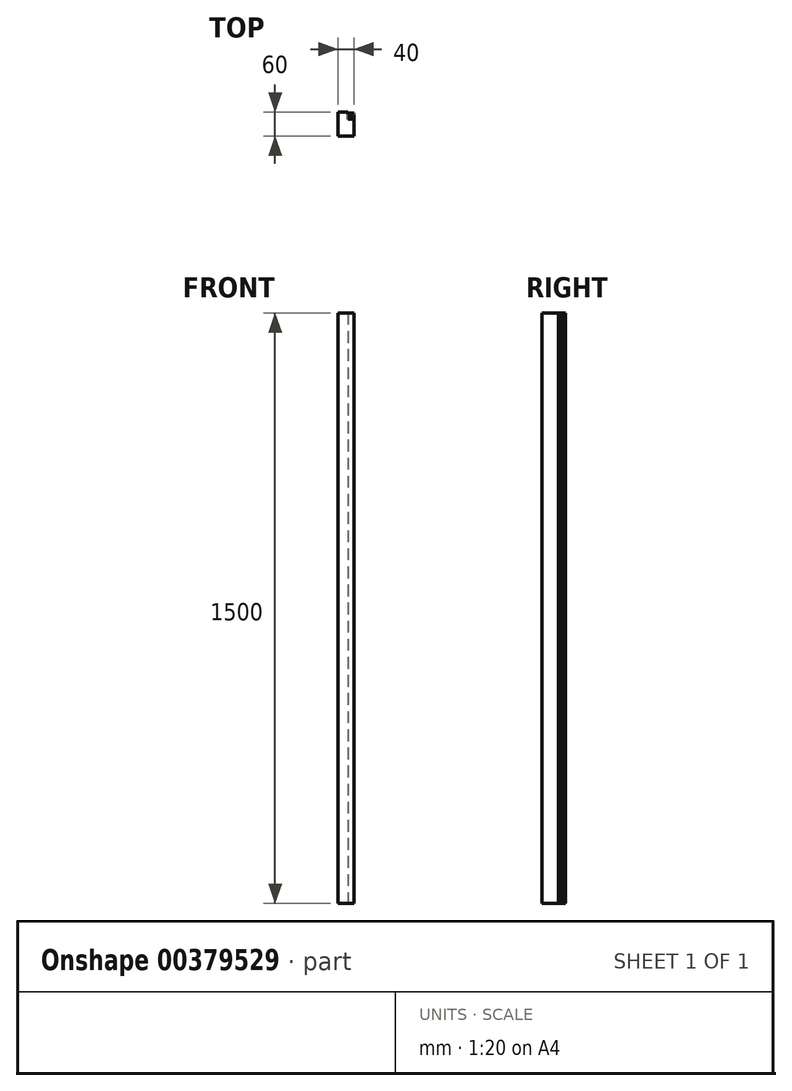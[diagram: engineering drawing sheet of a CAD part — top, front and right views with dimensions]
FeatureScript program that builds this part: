
annotation { "Feature Type Name" : "Feature", "Feature Type Description" : "" }
export const myFeature = defineFeature(function(context is Context, id is Id, definition is map)
    precondition{}
    {
        {
            var Q0;
            Q0=qCreatedBy(makeId("Top.planeOp"),FACE);
            var sketch = newSketch(context, id + "F0", { "sketchPlane" : qUnion([Q0])});
            skLineSegment(sketch, "E0.bottom", {"start": v(-20, -30) * mm, "end": v(20, -30) * mm});
            skLineSegment(sketch, "E0.top", {"start": v(-20, 30) * mm, "end": v(5, 30) * mm});
            skLineSegment(sketch, "E0.left", {"start": v(-20, -30) * mm, "end": v(-20, 30) * mm});
            skLineSegment(sketch, "E0.right", {"start": v(20, -30) * mm, "end": v(20, 12) * mm});
            skPoint(sketch, "E0.middle", {"position": v(0, 0) * mm});
            skLineSegment(sketch, "E1", {"start": v(20, 26) * mm, "end": v(5, 26) * mm});
            skLineSegment(sketch, "E2", {"start": v(5, 20) * mm, "end": v(20, 20) * mm});
            skLineSegment(sketch, "E3", {"start": v(20, 22) * mm, "end": v(5, 22) * mm});
            skLineSegment(sketch, "E4", {"start": v(20, 24) * mm, "end": v(5, 24) * mm});
            skLineSegment(sketch, "E5.MirrorCS", {"start": v(20, 14) * mm, "end": v(5, 14) * mm});
            skLineSegment(sketch, "E6.MirrorCS", {"start": v(20, 16) * mm, "end": v(5, 16) * mm});
            skLineSegment(sketch, "E7.MirrorCS", {"start": v(5, 18) * mm, "end": v(20, 18) * mm});
            skLineSegment(sketch, "E8.MirrorCS", {"start": v(20, 12) * mm, "end": v(5, 12) * mm});
            skLineSegment(sketch, "E9", {"start": v(5, 26) * mm, "end": v(5, 24) * mm});
            skLineSegment(sketch, "E10", {"start": v(5, 22) * mm, "end": v(5, 20) * mm});
            skLineSegment(sketch, "E11", {"start": v(5, 18) * mm, "end": v(5, 16) * mm});
            skLineSegment(sketch, "E12", {"start": v(5, 14) * mm, "end": v(5, 12) * mm});
            skLineSegment(sketch, "E13", {"start": v(5, 24) * mm, "end": v(5, 22) * mm, "construction": true});
            skLineSegment(sketch, "E14", {"start": v(5, 20) * mm, "end": v(5, 18) * mm, "construction": true});
            skLineSegment(sketch, "E15", {"start": v(5, 16) * mm, "end": v(5, 14) * mm, "construction": true});
            skLineSegment(sketch, "E16", {"start": v(20, 28) * mm, "end": v(5, 28) * mm});
            skLineSegment(sketch, "E17", {"start": v(5, 28) * mm, "end": v(5, 30) * mm});
            skLineSegment(sketch, "E18", {"start": v(5, 28) * mm, "end": v(5, 26) * mm, "construction": true});
            skPoint(sketch, "E19.orphan", {"position": v(20, 30) * mm});
            skLineSegment(sketch, "E20.trimOffspring", {"start": v(20, 26) * mm, "end": v(20, 28) * mm});
            skLineSegment(sketch, "E21.trimOffspring", {"start": v(20, 22) * mm, "end": v(20, 24) * mm});
            skLineSegment(sketch, "E22.trimOffspring", {"start": v(20, 18) * mm, "end": v(20, 20) * mm});
            skLineSegment(sketch, "E23.trimOffspring", {"start": v(20, 14) * mm, "end": v(20, 16) * mm});
            skSolve(sketch);
        }
        {
            var Q0;
            {var subQ9=sQuery(id+"F0.wireOp",EDGE,"E0.bottom");Q0=makeQuery(id+"F0.imprint","IMPRINT",FACE,{"disambiguationData":[TD([[makeQuery(id+"F0.imprint","IMPRINT",EDGE,{"derivedFrom":subQ9}),1.0]])]});}
            extrude(context, id + "F1", {"entities" : qUnion([Q0]), "depth" : 1500 * mm});
        }
    });
